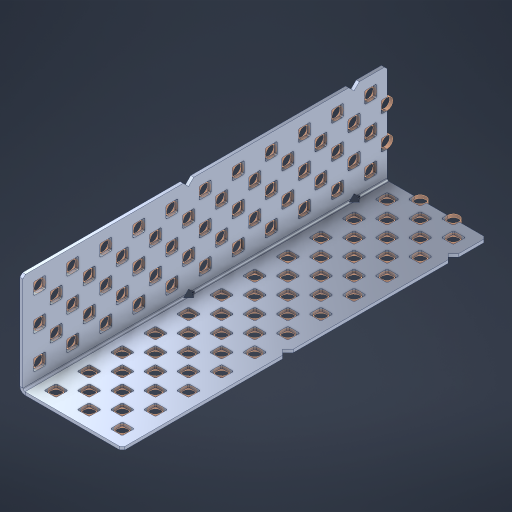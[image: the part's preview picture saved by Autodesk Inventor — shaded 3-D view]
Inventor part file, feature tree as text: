
AUTODESK INVENTOR PART (.ipt)
format: ipt  version: 2023 (Build 270158000, 158)  size: 1,422,336 bytes
history: native  units: in
note: dims shown in document units (in); Inventor stores cm internally (conversion verified against a paired STEP export)
features: other x116, extrude x108, sheet_metal_op x8, sketch x7, pattern_linear x3, mirror x1, chamfer x1
ambient origin geometry x8: Origin, YZ Plane, XZ Plane, XY Plane, X Axis, Y Axis, Z Axis, Center Point
bodies: Solid1 (feature_tree), Body (feature_tree)
feature tree (244):
  sheet_metal_op  "Flanges"
  sheet_metal_op  "Body Pattern"
  pattern_linear  "Center Double"  Spacing1=1.5in  [1 undecoded]
  pattern_linear  "Center Pattern"  Spacing1=0.1875in  [1 undecoded]
  other  "Arc Length"
  pattern_linear  "Notch Pattern"  Spacing1=0.0469in  [1 undecoded]
  other  "Diagonal Plane"
  mirror  "Everything Mirrored"
  chamfer  "End Chamfer"
  sketch  "Sketch1"  dims[d0=1.5in]
  other  "Plate1"
  sketch  "Sketch2"  dims[d1=5.5in]
  other  "Plate2"
  sheet_metal_op  "Bend1"
  sheet_metal_op  "Corner1"
  sketch  "Sketch8"  dims[d2=0.0469in]
  sketch  "Sketch9"  dims[d3=0.0469in]
  other  "Srf91"
  sheet_metal_op  "Body Pattern Sketch"
  other  "Srf92"
  sketch  "Sketch13"  dims[d4=0.0234in]
  sketch  "Sketch15"  dims[d5=0.0938in]
  sketch  "Sketch16"  dims[d6=0.0469in d7=1.5in d8=90.0deg d9=0.0312in d10=0.1875in d11=0.0469in d12=0.0469in d49=0.182in d50=0.02in d52=0.25in d53=0.0469in d54=0.0in d55=0.172in d56=1.0in d57=0.0in d85=0.1473in d86=0.1659in d89=0.0469in d90=0.0in d91=0.04in d92=0.0491in d95=2.5in d96=0.04in d97=0.25in d98=45.0deg d106=0.182in d107=0.02in d110=0.0469in d111=0.0in d112=0.172in d113=0.5in d114=0.0in d117=0.5in d126=0.0491in d127=0.1227in d128=0.08in d129=0.04in d130=2.5in d131=0.25in d132=4.3307in d134=0.5in d135=1.1811in d137=0.5in d140=0.5in d141=1.0in d142=0.3937in d144=0.5in d145=0.071in d146=0.7874in d148=0.5in]
  other  "Srf786"
  other  "Srf856"
  other  "Srf889"
  other  "Srf890"
  other  "Srf891"
  other  "Srf1275"
  other  "Srf1276"
  other  "Srf1278"
  other  "Srf1277"
  other  "Srf1285"
  other  "Srf1286"
  other  "Srf1287"
  other  "Srf1445"
  other  "Srf1446"
  other  "Srf1447"
  other  "Srf1448"
  other  "Srf1449"
  other  "Srf1537"
  other  "Srf1538"
  other  "Srf1539"
  other  "Srf1540"
  other  "Srf1541"
  other  "Srf1807"
  other  "Srf1808"
  other  "Srf1959"
  other  "Srf1960"
  other  "Srf2009"
  other  "Srf2010"
  other  "Srf2011"
  other  "Srf2012"
  other  "Srf2013"
  other  "Srf2014"
  other  "Srf2015"
  other  "Srf2016"
  other  "Srf2017"
  other  "Srf2018"
  other  "Srf2019"
  other  "Srf2043"
  other  "Srf2044"
  other  "Srf2045"
  other  "Srf2046"
  other  "Srf2047"
  other  "Srf2048"
  other  "Srf2049"
  other  "Srf2050"
  other  "Srf2051"
  other  "Srf2052"
  other  "Srf2076"
  other  "Srf2077"
  other  "Srf2078"
  other  "Srf2079"
  other  "Srf2080"
  other  "Srf2081"
  other  "Srf2082"
  other  "Srf2083"
  other  "Srf2084"
  other  "Srf2085"
  other  "Srf2086"
  other  "Srf2087"
  other  "Srf2088"
  other  "Srf2089"
  other  "Srf2090"
  other  "Srf2091"
  other  "Srf2092"
  other  "Srf2093"
  other  "Srf2094"
  other  "Srf2095"
  other  "Srf2096"
  other  "Srf2097"
  other  "Srf2098"
  other  "Srf2099"
  other  "Srf2100"
  other  "Srf2101"
  other  "Srf2102"
  other  "Srf2103"
  other  "Srf2104"
  other  "Srf2105"
  other  "Srf2106"
  other  "Srf2179"
  other  "Srf2180"
  other  "Srf2181"
  other  "Srf2182"
  other  "Srf2183"
  other  "Srf2184"
  other  "Srf2185"
  other  "Srf2186"
  other  "Srf2187"
  other  "Srf2188"
  other  "Srf2189"
  other  "Srf2190"
  other  "Srf2191"
  other  "Srf2192"
  other  "Srf2193"
  other  "Srf2194"
  other  "Srf2195"
  other  "Srf2196"
  other  "Srf2197"
  other  "Srf2198"
  other  "Srf2199"
  other  "Srf2200"
  other  "Srf2201"
  other  "Srf2202"
  other  "Srf2203"
  other  "Srf2204"
  other  "Srf2205"
  other  "Srf2206"
  other  "Srf2207"
  other  "Srf2208"
  sheet_metal_op  "Body Stamp"
  sheet_metal_op  "Body Circle"
  other  "Center Stamp"
  other  "Center Circle"
  sheet_metal_op  "Notch"
  extrude  "ExtrusionSrf92"  Depth=0.0469in
  extrude  "ExtrusionSrf856"  Depth=0.182in
  extrude  "ExtrusionSrf889"  Depth=0.02in
  extrude  "ExtrusionSrf890"  Depth=0.25in
  extrude  "ExtrusionSrf891"  Depth=0.0469in
  extrude  "ExtrusionSrf1275"  TaperAngle=0.0deg  [1 undecoded]
  extrude  "ExtrusionSrf1276"  Depth=0.5in
  extrude  "ExtrusionSrf1277"  Depth=1.0in TaperAngle=0.0deg
  extrude  "ExtrusionSrf1345"  Depth=0.5in
  extrude  "ExtrusionSrf1346"  Depth=0.5in
  extrude  "ExtrusionSrf1347"  Depth=0.0469in
  extrude  "ExtrusionSrf1348"  Depth=0.5in TaperAngle=0.0deg
  extrude  "ExtrusionSrf1445"  Depth=0.5in
  extrude  "ExtrusionSrf1446"  Depth=0.25in TaperAngle=45.0deg
  extrude  "ExtrusionSrf1447"  Depth=0.182in
  extrude  "ExtrusionSrf1448"  Depth=0.02in
  extrude  "ExtrusionSrf1449"  Depth=0.0469in
  extrude  "ExtrusionSrf1537"  TaperAngle=0.0deg  [1 undecoded]
  extrude  "ExtrusionSrf1538"  Depth=0.5in
  extrude  "ExtrusionSrf1539"  Depth=0.5in TaperAngle=0.0deg
  extrude  "ExtrusionSrf1540"  Depth=0.5in
  extrude  "ExtrusionSrf1541"  Depth=0.5in
  extrude  "ExtrusionSrf1807"  Depth=0.5in
  extrude  "ExtrusionSrf1808"  Depth=0.5in
  extrude  "ExtrusionSrf1959"  Depth=0.5in
  extrude  "ExtrusionSrf1960"  Depth=0.5in
  extrude  "ExtrusionSrf2009"  Depth=0.25in
  extrude  "ExtrusionSrf2010"  Depth=0.5in
  extrude  "ExtrusionSrf2011"  Depth=0.5in
  extrude  "ExtrusionSrf2012"  Depth=0.5in
  extrude  "ExtrusionSrf2013"  Depth=1.0in
  extrude  "ExtrusionSrf2014"  Depth=0.3937in
  extrude  "ExtrusionSrf2015"  Depth=0.5in
  extrude  "ExtrusionSrf2016"  Depth=0.5in
  extrude  "ExtrusionSrf2017"  [1 undecoded]
  extrude  "ExtrusionSrf2018"  [1 undecoded]
  extrude  "ExtrusionSrf2019"  [1 undecoded]
  extrude  "ExtrusionSrf2043"  [1 undecoded]
  extrude  "ExtrusionSrf2044"  [1 undecoded]
  extrude  "ExtrusionSrf2045"  [1 undecoded]
  extrude  "ExtrusionSrf2046"  [1 undecoded]
  extrude  "ExtrusionSrf2047"  [1 undecoded]
  extrude  "ExtrusionSrf2048"  [1 undecoded]
  extrude  "ExtrusionSrf2049"  [1 undecoded]
  extrude  "ExtrusionSrf2050"  [1 undecoded]
  extrude  "ExtrusionSrf2051"  [1 undecoded]
  extrude  "ExtrusionSrf2052"  [1 undecoded]
  extrude  "ExtrusionSrf2076"  [1 undecoded]
  extrude  "ExtrusionSrf2077"  [1 undecoded]
  extrude  "ExtrusionSrf2078"  [1 undecoded]
  extrude  "ExtrusionSrf2079"  [1 undecoded]
  extrude  "ExtrusionSrf2080"  [1 undecoded]
  extrude  "ExtrusionSrf2081"  [1 undecoded]
  extrude  "ExtrusionSrf2082"  [1 undecoded]
  extrude  "ExtrusionSrf2083"  [1 undecoded]
  extrude  "ExtrusionSrf2084"  [1 undecoded]
  extrude  "ExtrusionSrf2085"  [1 undecoded]
  extrude  "ExtrusionSrf2086"  [1 undecoded]
  extrude  "ExtrusionSrf2087"  [1 undecoded]
  extrude  "ExtrusionSrf2088"  [1 undecoded]
  extrude  "ExtrusionSrf2089"  [1 undecoded]
  extrude  "ExtrusionSrf2090"  [1 undecoded]
  extrude  "ExtrusionSrf2091"  [1 undecoded]
  extrude  "ExtrusionSrf2092"  [1 undecoded]
  extrude  "ExtrusionSrf2093"  [1 undecoded]
  extrude  "ExtrusionSrf2094"  [1 undecoded]
  extrude  "ExtrusionSrf2095"  [1 undecoded]
  extrude  "ExtrusionSrf2096"  [1 undecoded]
  extrude  "ExtrusionSrf2097"  [1 undecoded]
  extrude  "ExtrusionSrf2098"  [1 undecoded]
  extrude  "ExtrusionSrf2099"  [1 undecoded]
  extrude  "ExtrusionSrf2100"  [1 undecoded]
  extrude  "ExtrusionSrf2101"  [1 undecoded]
  extrude  "ExtrusionSrf2102"  [1 undecoded]
  extrude  "ExtrusionSrf2103"  [1 undecoded]
  extrude  "ExtrusionSrf2104"  [1 undecoded]
  extrude  "ExtrusionSrf2105"  [1 undecoded]
  extrude  "ExtrusionSrf2106"  [1 undecoded]
  extrude  "ExtrusionSrf2179"  [1 undecoded]
  extrude  "ExtrusionSrf2180"  [1 undecoded]
  extrude  "ExtrusionSrf2181"  [1 undecoded]
  extrude  "ExtrusionSrf2182"  [1 undecoded]
  extrude  "ExtrusionSrf2183"  [1 undecoded]
  extrude  "ExtrusionSrf2184"  [1 undecoded]
  extrude  "ExtrusionSrf2185"  [1 undecoded]
  extrude  "ExtrusionSrf2186"  [1 undecoded]
  extrude  "ExtrusionSrf2187"  [1 undecoded]
  extrude  "ExtrusionSrf2188"  [1 undecoded]
  extrude  "ExtrusionSrf2189"  [1 undecoded]
  extrude  "ExtrusionSrf2190"  [1 undecoded]
  extrude  "ExtrusionSrf2191"  [1 undecoded]
  extrude  "ExtrusionSrf2192"  [1 undecoded]
  extrude  "ExtrusionSrf2193"  [1 undecoded]
  extrude  "ExtrusionSrf2194"  [1 undecoded]
  extrude  "ExtrusionSrf2195"  [1 undecoded]
  extrude  "ExtrusionSrf2196"  [1 undecoded]
  extrude  "ExtrusionSrf2197"  [1 undecoded]
  extrude  "ExtrusionSrf2198"  [1 undecoded]
  extrude  "ExtrusionSrf2199"  [1 undecoded]
  extrude  "ExtrusionSrf2200"  [1 undecoded]
  extrude  "ExtrusionSrf2201"  [1 undecoded]
  extrude  "ExtrusionSrf2202"  [1 undecoded]
  extrude  "ExtrusionSrf2203"  [1 undecoded]
  extrude  "ExtrusionSrf2204"  [1 undecoded]
  extrude  "ExtrusionSrf2205"  [1 undecoded]
  extrude  "ExtrusionSrf2206"  [1 undecoded]
  extrude  "ExtrusionSrf2207"  [1 undecoded]
  extrude  "ExtrusionSrf2208"  [1 undecoded]
note: 79 required parameter values undecoded (feature->parameter linkage not recoverable at this tier; creation-order binding heuristic only, values carry confidence <= 0.55)
